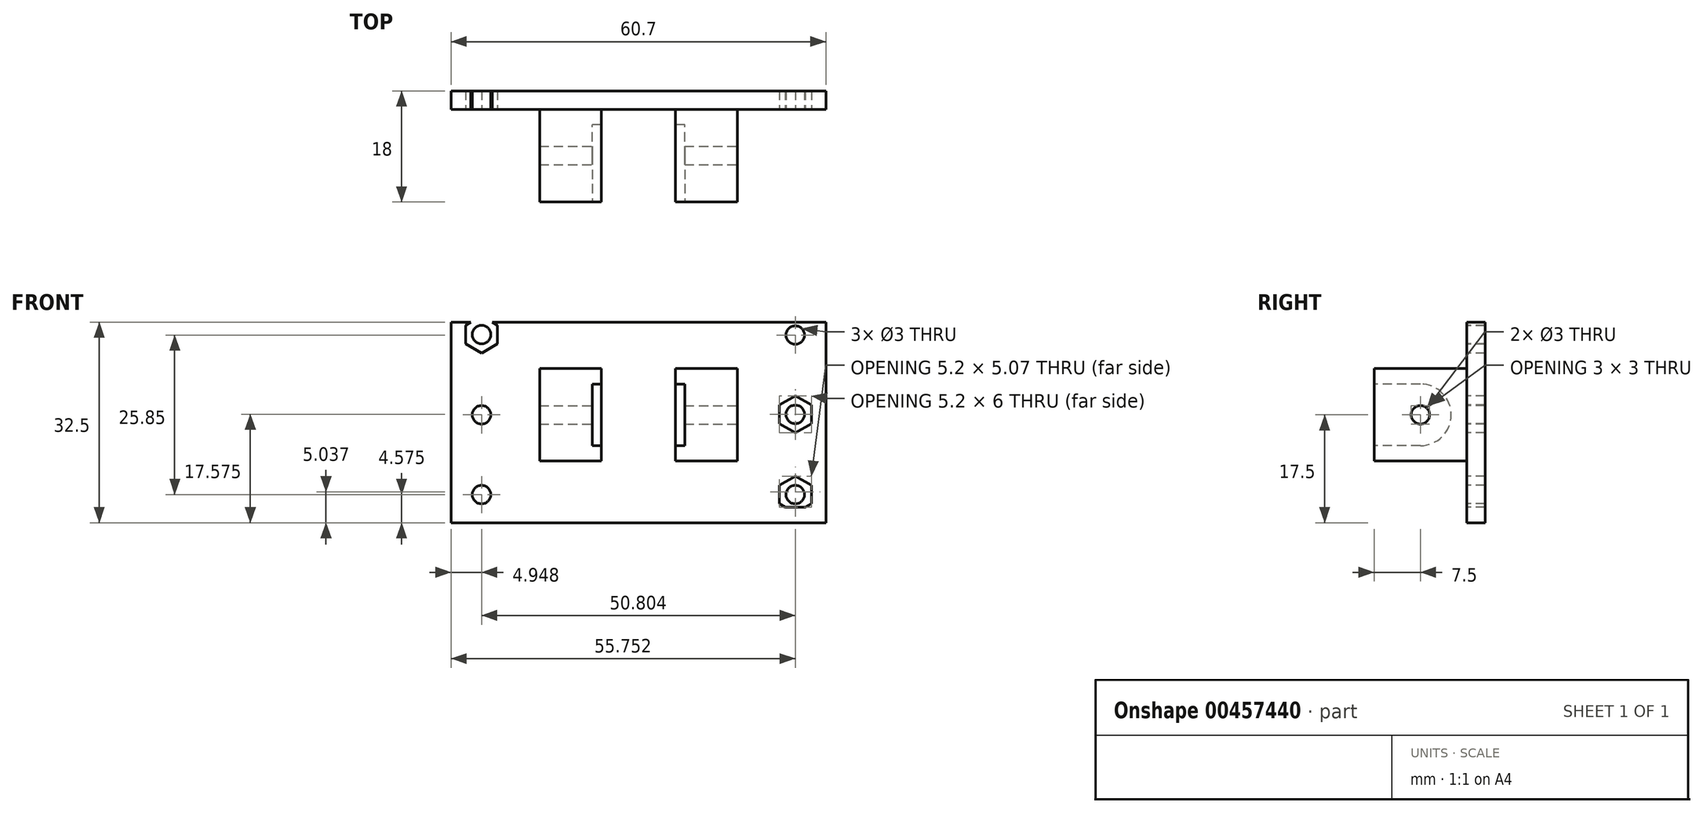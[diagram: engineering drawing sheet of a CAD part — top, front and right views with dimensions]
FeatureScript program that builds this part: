
annotation { "Feature Type Name" : "Feature", "Feature Type Description" : "" }
export const myFeature = defineFeature(function(context is Context, id is Id, definition is map)
    precondition{}
    {
        {
            var Q0;
            Q0=qCreatedBy(makeId("Front.planeOp"),FACE);
            var sketch = newSketch(context, id + "F0", { "sketchPlane" : qUnion([Q0])});
            skLineSegment(sketch, "E0.bottom", {"start": v(30, 15) * mm, "end": v(-30, 15) * mm});
            skLineSegment(sketch, "E0.top", {"start": v(30, -15) * mm, "end": v(-30, -15) * mm});
            skLineSegment(sketch, "E0.left", {"start": v(30, 15) * mm, "end": v(30, -15) * mm});
            skLineSegment(sketch, "E0.right", {"start": v(-30, 15) * mm, "end": v(-30, -15) * mm});
            skPoint(sketch, "E0.middle", {"position": v(0, 0) * mm});
            skSolve(sketch);
        }
        {
            var Q0;
            Q0=makeQuery(id+"F0.imprint","IMPRINT",FACE,{"disambiguationData":[TD([[makeQuery(id+"F0.imprint","IMPRINT",EDGE,{"derivedFrom":sQuery(id+"F0.wireOp",EDGE,"E0.bottom")}),1.0]])]});
            extrude(context, id + "F1", {"entities" : qUnion([Q0]), "endBound" : BoundingType.SYMMETRIC, "depth" : 3 * mm});
        }
        {
            var Q0;
            Q0=makeQuery(id+"F1.opExtrude","CAP_FACE",FACE,{"disambiguationData":[OSD([sQuery(id+"F0.wireOp",EDGE,"E0.bottom"),sQuery(id+"F0.wireOp",EDGE,"E0.top"),sQuery(id+"F0.wireOp",EDGE,"E0.left"),sQuery(id+"F0.wireOp",EDGE,"E0.right")])],"isStart":false});
            var sketch = newSketch(context, id + "F2", { "sketchPlane" : qUnion([Q0])});
            skCircle(sketch, "E1", {"center": v(-162.2, 7.5) * mm, "radius": 1.5 * mm});
            skCircle(sketch, "E2.MirrorC", {"center": v(-162.2, -7.5) * mm, "radius": 1.5 * mm});
            skLineSegment(sketch, "E3.0", {"start": v(-162.2, 10.5) * mm, "end": v(-159.6, 9) * mm});
            skLineSegment(sketch, "E3.1", {"start": v(-159.6, 9) * mm, "end": v(-159.6, 6) * mm});
            skLineSegment(sketch, "E3.2", {"start": v(-159.6, 6) * mm, "end": v(-162.2, 4.5) * mm});
            skLineSegment(sketch, "E3.3", {"start": v(-162.2, 4.5) * mm, "end": v(-164.8, 6) * mm});
            skLineSegment(sketch, "E3.4", {"start": v(-164.8, 6) * mm, "end": v(-164.8, 9) * mm});
            skLineSegment(sketch, "E3.5", {"start": v(-164.8, 9) * mm, "end": v(-162.2, 10.5) * mm});
            skLineSegment(sketch, "E4.MirrorCS", {"start": v(-162.2, -4.5) * mm, "end": v(-164.8, -6) * mm});
            skLineSegment(sketch, "E5.MirrorCS", {"start": v(-162.2, -10.5) * mm, "end": v(-159.6, -9) * mm});
            skLineSegment(sketch, "E6.MirrorCS", {"start": v(-164.8, -9) * mm, "end": v(-162.2, -10.5) * mm});
            skLineSegment(sketch, "E7.MirrorCS", {"start": v(-159.6, -9) * mm, "end": v(-159.6, -6) * mm});
            skLineSegment(sketch, "E8.MirrorCS", {"start": v(-164.8, -6) * mm, "end": v(-164.8, -9) * mm});
            skLineSegment(sketch, "E9.MirrorCS", {"start": v(-159.6, -6) * mm, "end": v(-162.2, -4.5) * mm});
            skLineSegment(sketch, "E10.MirrorCS", {"start": v(-162.2, 3) * mm, "end": v(-159.6, 1.5) * mm});
            skCircle(sketch, "E11.MirrorC", {"center": v(-162.2, 0) * mm, "radius": 1.5 * mm});
            skLineSegment(sketch, "E12.MirrorCS", {"start": v(-159.6, 1.5) * mm, "end": v(-159.6, -1.5) * mm});
            skLineSegment(sketch, "E13.MirrorCS", {"start": v(-162.2, -3) * mm, "end": v(-164.8, -1.5) * mm});
            skLineSegment(sketch, "E14.MirrorCS", {"start": v(-164.8, -1.5) * mm, "end": v(-164.8, 1.5) * mm});
            skLineSegment(sketch, "E15.MirrorCS", {"start": v(-159.6, -1.5) * mm, "end": v(-162.2, -3) * mm});
            skLineSegment(sketch, "E16.MirrorCS", {"start": v(-164.8, 1.5) * mm, "end": v(-162.2, 3) * mm});
            skLineSegment(sketch, "E17.MirrorCS", {"start": v(-22.8, 14.5) * mm, "end": v(-25.4, 16) * mm});
            skLineSegment(sketch, "E18.MirrorCS", {"start": v(-28, 11.5) * mm, "end": v(-25.4, 10) * mm});
            skLineSegment(sketch, "E19.MirrorCS", {"start": v(-25.4, -9.92) * mm, "end": v(-22.8, -11.42) * mm});
            skLineSegment(sketch, "E20.MirrorCS", {"start": v(-28, -11.42) * mm, "end": v(-25.4, -9.92) * mm});
            skLineSegment(sketch, "E21.MirrorCS", {"start": v(-25.4, -15.93) * mm, "end": v(-28, -14.43) * mm});
            skLineSegment(sketch, "E22.MirrorCS", {"start": v(-22.8, -14.43) * mm, "end": v(-25.4, -15.93) * mm});
            skLineSegment(sketch, "E23.MirrorCS", {"start": v(-25.4, 10) * mm, "end": v(-22.8, 11.5) * mm});
            skLineSegment(sketch, "E24.MirrorCS", {"start": v(-25.4, 16) * mm, "end": v(-28, 14.5) * mm});
            skLineSegment(sketch, "E25.MirrorCS", {"start": v(-22.8, 11.5) * mm, "end": v(-22.8, 14.5) * mm});
            skCircle(sketch, "E26.MirrorC", {"center": v(-25.4, 13) * mm, "radius": 1.5 * mm});
            skLineSegment(sketch, "E27.MirrorCS", {"start": v(-22.8, -11.42) * mm, "end": v(-22.8, -14.42) * mm});
            skLineSegment(sketch, "E28.MirrorCS", {"start": v(-28, 14.5) * mm, "end": v(-28, 11.5) * mm});
            skLineSegment(sketch, "E29.MirrorCS", {"start": v(-28, -14.42) * mm, "end": v(-28, -11.43) * mm});
            skCircle(sketch, "E30.MirrorC", {"center": v(-25.4, -12.92) * mm, "radius": 1.5 * mm});
            skPoint(sketch, "E31.endSnap0", {"position": v(-30, 0) * mm});
            skLineSegment(sketch, "E32.MirrorCS", {"start": v(25.4, 15.93) * mm, "end": v(28, 14.43) * mm});
            skLineSegment(sketch, "E33.MirrorCS", {"start": v(28, -11.42) * mm, "end": v(25.4, -9.92) * mm});
            skCircle(sketch, "E34.MirrorC", {"center": v(25.4, 12.93) * mm, "radius": 1.5 * mm});
            skLineSegment(sketch, "E35.MirrorCS", {"start": v(22.8, 14.43) * mm, "end": v(25.4, 15.93) * mm});
            skLineSegment(sketch, "E36.MirrorCS", {"start": v(25.4, 9.92) * mm, "end": v(22.8, 11.42) * mm});
            skLineSegment(sketch, "E37.MirrorCS", {"start": v(25.4, -9.92) * mm, "end": v(22.8, -11.42) * mm});
            skLineSegment(sketch, "E38.MirrorCS", {"start": v(28, -14.42) * mm, "end": v(28, -11.43) * mm});
            skLineSegment(sketch, "E39.MirrorCS", {"start": v(22.8, 11.42) * mm, "end": v(22.8, 14.42) * mm});
            skLineSegment(sketch, "E40.MirrorCS", {"start": v(25.4, -15.93) * mm, "end": v(28, -14.43) * mm});
            skLineSegment(sketch, "E41.MirrorCS", {"start": v(22.8, -11.42) * mm, "end": v(22.8, -14.42) * mm});
            skLineSegment(sketch, "E42.MirrorCS", {"start": v(28, 14.43) * mm, "end": v(28, 11.43) * mm});
            skLineSegment(sketch, "E43.MirrorCS", {"start": v(28, 11.42) * mm, "end": v(25.4, 9.92) * mm});
            skCircle(sketch, "E44.MirrorC", {"center": v(25.4, -12.92) * mm, "radius": 1.5 * mm});
            skLineSegment(sketch, "E45.MirrorCS", {"start": v(22.8, -14.43) * mm, "end": v(25.4, -15.93) * mm});
            skPoint(sketch, "E46.MirrorP", {"position": v(30, 0) * mm});
            skLineSegment(sketch, "E47.bottom", {"start": v(-6, 7.5) * mm, "end": v(6, 7.5) * mm});
            skLineSegment(sketch, "E47.top", {"start": v(-6, -7.5) * mm, "end": v(6, -7.5) * mm});
            skLineSegment(sketch, "E47.left", {"start": v(-6, 7.5) * mm, "end": v(-6, -7.5) * mm});
            skLineSegment(sketch, "E47.right", {"start": v(6, 7.5) * mm, "end": v(6, -7.5) * mm});
            skPoint(sketch, "E47.middle", {"position": v(0, 0) * mm});
            skLineSegment(sketch, "E48.bottom", {"start": v(6, -7.5) * mm, "end": v(16, -7.5) * mm});
            skLineSegment(sketch, "E48.top", {"start": v(6, 7.5) * mm, "end": v(16, 7.5) * mm});
            skLineSegment(sketch, "E48.left", {"start": v(6, -7.5) * mm, "end": v(6, 7.5) * mm});
            skLineSegment(sketch, "E48.right", {"start": v(16, -7.5) * mm, "end": v(16, 7.5) * mm});
            skLineSegment(sketch, "E49.MirrorCS", {"start": v(-6, -7.5) * mm, "end": v(-6, 7.5) * mm});
            skLineSegment(sketch, "E50.MirrorCS", {"start": v(-6, 7.5) * mm, "end": v(-16, 7.5) * mm});
            skLineSegment(sketch, "E51.MirrorCS", {"start": v(-16, -7.5) * mm, "end": v(-16, 7.5) * mm});
            skLineSegment(sketch, "E52.MirrorCS", {"start": v(-6, -7.5) * mm, "end": v(-16, -7.5) * mm});
            skLineSegment(sketch, "E53", {"start": v(-25.4, 17.5) * mm, "end": v(-25.4, 12.93) * mm});
            skLineSegment(sketch, "E54", {"start": v(-25.4, -17.5) * mm, "end": v(-25.4, -12.92) * mm});
            skLineSegment(sketch, "E55", {"start": v(-25.4, 0) * mm, "end": v(-25.4, 13) * mm});
            skLineSegment(sketch, "E56", {"start": v(-25.4, 6.5) * mm, "end": v(-21.98, 6.5) * mm});
            skLineSegment(sketch, "E57.MirrorCS", {"start": v(28, -1.42) * mm, "end": v(28, 1.58) * mm});
            skLineSegment(sketch, "E58.MirrorCS", {"start": v(22.8, 1.58) * mm, "end": v(22.8, -1.42) * mm});
            skLineSegment(sketch, "E59.MirrorCS", {"start": v(28, 1.58) * mm, "end": v(25.4, 3.08) * mm});
            skLineSegment(sketch, "E60.MirrorCS", {"start": v(25.4, -2.92) * mm, "end": v(28, -1.42) * mm});
            skLineSegment(sketch, "E61.MirrorCS", {"start": v(25.4, 3.08) * mm, "end": v(22.8, 1.58) * mm});
            skLineSegment(sketch, "E62.MirrorCS", {"start": v(22.8, -1.42) * mm, "end": v(25.4, -2.93) * mm});
            skCircle(sketch, "E63.MirrorC", {"center": v(25.4, 0.08) * mm, "radius": 1.5 * mm});
            skLineSegment(sketch, "E64.MirrorCS", {"start": v(-22.8, -1.5) * mm, "end": v(-25.4, -3) * mm});
            skLineSegment(sketch, "E65.MirrorCS", {"start": v(-25.4, -3) * mm, "end": v(-28, -1.5) * mm});
            skCircle(sketch, "E66.MirrorC", {"center": v(-25.4, 0) * mm, "radius": 1.5 * mm});
            skLineSegment(sketch, "E67.MirrorCS", {"start": v(-28, -1.5) * mm, "end": v(-28, 1.5) * mm});
            skLineSegment(sketch, "E68.MirrorCS", {"start": v(-25.4, 3) * mm, "end": v(-22.8, 1.5) * mm});
            skLineSegment(sketch, "E69.MirrorCS", {"start": v(-22.8, 1.5) * mm, "end": v(-22.8, -1.5) * mm});
            skLineSegment(sketch, "E70.MirrorCS", {"start": v(-28, 1.5) * mm, "end": v(-25.4, 3) * mm});
            skSolve(sketch);
        }
        {
            var Q0;
            Q0=makeQuery(id+"F2.imprint","IMPRINT",FACE,{"disambiguationData":[TD([[makeQuery(id+"F2.imprint","IMPRINT",EDGE,{"derivedFrom":sQuery(id+"F2.wireOp",EDGE,"E50.MirrorCS")}),1.0]])]});
            var Q1;
            Q1=makeQuery(id+"F2.imprint","IMPRINT",FACE,{"disambiguationData":[TD([[makeQuery(id+"F2.imprint","IMPRINT",EDGE,{"derivedFrom":sQuery(id+"F2.wireOp",EDGE,"E48.bottom")}),1.0]])]});
            extrude(context, id + "F3", {"entities" : qUnion([Q0, Q1]), "operationType" : NewBodyOperationType.ADD, "depth" : 15 * mm});
        }
        {
            var Q0;
            Q0=makeQuery(id+"F2.imprint","IMPRINT",FACE,{"disambiguationData":[TD([[makeQuery(id+"F2.imprint","IMPRINT",EDGE,{"derivedFrom":sQuery(id+"F2.wireOp",EDGE,"E26.MirrorC")}),-1.0]])]});
            var Q1;
            Q1=makeQuery(id+"F2.imprint","IMPRINT",FACE,{"disambiguationData":[TD([[makeQuery(id+"F2.imprint","IMPRINT",EDGE,{"derivedFrom":sQuery(id+"F2.wireOp",EDGE,"E30.MirrorC")}),1.0]])]});
            var Q2;
            Q2=makeQuery(id+"F2.imprint","IMPRINT",FACE,{"disambiguationData":[TD([[makeQuery(id+"F2.imprint","IMPRINT",EDGE,{"derivedFrom":sQuery(id+"F2.wireOp",EDGE,"E34.MirrorC")}),1.0]])]});
            var Q3;
            Q3=makeQuery(id+"F2.imprint","IMPRINT",FACE,{"disambiguationData":[TD([[makeQuery(id+"F2.imprint","IMPRINT",EDGE,{"derivedFrom":sQuery(id+"F2.wireOp",EDGE,"E44.MirrorC")}),-1.0]])]});
            var Q4;
            Q4=makeQuery(id+"F2.imprint","IMPRINT",FACE,{"disambiguationData":[TD([[makeQuery(id+"F2.imprint","IMPRINT",EDGE,{"derivedFrom":sQuery(id+"F2.wireOp",EDGE,"E66.MirrorC")}),1.0]])]});
            var Q5;
            Q5=makeQuery(id+"F2.imprint","IMPRINT",FACE,{"disambiguationData":[TD([[makeQuery(id+"F2.imprint","IMPRINT",EDGE,{"derivedFrom":sQuery(id+"F2.wireOp",EDGE,"E63.MirrorC")}),-1.0]])]});
            extrude(context, id + "F4", {"entities" : qUnion([Q0, Q1, Q2, Q3, Q4, Q5]), "operationType" : NewBodyOperationType.REMOVE, "oppositeDirection" : true, "depth" : 3 * mm});
        }
        {
            var Q0;
            Q0=qCreatedBy(makeId("Right.planeOp"),FACE);
            var sketch = newSketch(context, id + "F5", { "sketchPlane" : qUnion([Q0])});
            skPoint(sketch, "E71.0", {"position": v(-16.5, 0) * mm});
            skPoint(sketch, "E72.0", {"position": v(-9, 7.5) * mm});
            skCircle(sketch, "E73", {"center": v(-9, 0) * mm, "radius": 1.5 * mm});
            skCircle(sketch, "E74", {"center": v(-9, 0) * mm, "radius": 5 * mm});
            skSolve(sketch);
        }
        {
            var Q0;
            Q0=makeQuery(id+"F5.imprint","IMPRINT",FACE,{"disambiguationData":[TD([[makeQuery(id+"F5.imprint","IMPRINT",EDGE,{"derivedFrom":sQuery(id+"F5.wireOp",EDGE,"E73")}),-1.0]])]});
            extrude(context, id + "F6", {"entities" : qUnion([Q0]), "operationType" : NewBodyOperationType.REMOVE, "endBound" : BoundingType.SYMMETRIC, "depth" : 15 * mm});
        }
        {
            var Q0;
            Q0=makeQuery(id+"F6.boolean.opBoolean","SPLIT",FACE,{"disambiguationData":[TD([makeQuery(id+"F6.opExtrude","SWEPT_FACE",FACE,{"disambiguationData":[OSD([sQuery(id+"F5.wireOp",EDGE,"E73")])]})])],"derivedFrom":makeQuery(id+"F3.opExtrude","SWEPT_FACE",FACE,{"disambiguationData":[OSD([sQuery(id+"F2.wireOp",EDGE,"E47.left")])]})});
            extrude(context, id + "F7", {"entities" : qUnion([Q0]), "operationType" : NewBodyOperationType.REMOVE, "endBound" : BoundingType.SYMMETRIC, "oppositeDirection" : true, "depth" : 60 * mm});
        }
        {
            var Q0;
            Q0=qCreatedBy(makeId("Right.planeOp"),FACE);
            var sketch = newSketch(context, id + "F8", { "sketchPlane" : qUnion([Q0])});
            skLineSegment(sketch, "E75.0", {"start": v(-16.5, 5) * mm, "end": v(-16.5, -5) * mm});
            skLineSegment(sketch, "E76", {"start": v(-9, 0) * mm, "end": v(-9, 5) * mm});
            skLineSegment(sketch, "E77", {"start": v(-9, 5) * mm, "end": v(-16.5, 5) * mm});
            skLineSegment(sketch, "E78", {"start": v(-9, 0) * mm, "end": v(-9, -5) * mm});
            skLineSegment(sketch, "E79", {"start": v(-9, -5) * mm, "end": v(-16.5, -5) * mm});
            skSolve(sketch);
        }
        {
            var Q0;
            Q0=makeQuery(id+"F8.imprint","IMPRINT",FACE,{"disambiguationData":[TD([[makeQuery(id+"F8.imprint","IMPRINT",EDGE,{"derivedFrom":sQuery(id+"F8.wireOp",EDGE,"E75.0")}),1.0]])]});
            extrude(context, id + "F9", {"entities" : qUnion([Q0]), "operationType" : NewBodyOperationType.REMOVE, "endBound" : BoundingType.SYMMETRIC, "oppositeDirection" : true, "depth" : 15 * mm});
        }
        {
            var Q0;
            Q0=makeQuery(id+"F1.opExtrude","CAP_FACE",FACE,{"disambiguationData":[OSD([sQuery(id+"F0.wireOp",EDGE,"E0.bottom"),sQuery(id+"F0.wireOp",EDGE,"E0.top"),sQuery(id+"F0.wireOp",EDGE,"E0.left"),sQuery(id+"F0.wireOp",EDGE,"E0.right")])],"isStart":true});
            var sketch = newSketch(context, id + "F10", { "sketchPlane" : qUnion([Q0])});
            skCircle(sketch, "E80.0", {"center": v(-25.4, -12.92) * mm, "radius": 1.5 * mm});
            skLineSegment(sketch, "E81.0", {"start": v(-30, 15) * mm, "end": v(-30, -15) * mm});
            skLineSegment(sketch, "E82", {"start": v(-25.4, -12.92) * mm, "end": v(-30.35, -12.92) * mm});
            skLineSegment(sketch, "E83.bottom", {"start": v(-30.35, -15) * mm, "end": v(-30, -15) * mm});
            skLineSegment(sketch, "E83.top", {"start": v(-30.35, 15) * mm, "end": v(-30, 15) * mm});
            skLineSegment(sketch, "E83.left", {"start": v(-30.35, -15) * mm, "end": v(-30.35, 15) * mm});
            skLineSegment(sketch, "E83.right", {"start": v(-30, -15) * mm, "end": v(-30, 15) * mm});
            skLineSegment(sketch, "E84", {"start": v(0, -15) * mm, "end": v(0, 0) * mm});
            skLineSegment(sketch, "E85.MirrorCS", {"start": v(30.35, -15) * mm, "end": v(30, -15) * mm});
            skLineSegment(sketch, "E86.MirrorCS", {"start": v(30.35, 15) * mm, "end": v(30, 15) * mm});
            skLineSegment(sketch, "E87.MirrorCS", {"start": v(30, 15) * mm, "end": v(30, -15) * mm});
            skLineSegment(sketch, "E88.MirrorCS", {"start": v(30, -15) * mm, "end": v(30, 15) * mm});
            skLineSegment(sketch, "E89.MirrorCS", {"start": v(30.35, -15) * mm, "end": v(30.35, 15) * mm});
            skLineSegment(sketch, "E90.0", {"start": v(-30, -15) * mm, "end": v(30, -15) * mm});
            skLineSegment(sketch, "E91.0", {"start": v(-30, 15) * mm, "end": v(30, 15) * mm});
            skLineSegment(sketch, "E92", {"start": v(-25.4, -15) * mm, "end": v(-25.4, -10.43) * mm});
            skSolve(sketch);
        }
        {
            var Q0;
            Q0=makeQuery(id+"F10.imprint","IMPRINT",FACE,{"disambiguationData":[TD([[makeQuery(id+"F10.imprint","IMPRINT",EDGE,{"derivedFrom":sQuery(id+"F10.wireOp",EDGE,"E85.MirrorCS")}),-1.0]])]});
            var Q1;
            {var subQ5=sQuery(id+"F10.wireOp",EDGE,"E83.bottom");Q1=makeQuery(id+"F10.imprint","IMPRINT",FACE,{"disambiguationData":[TD([[makeQuery(id+"F10.imprint","IMPRINT",EDGE,{"derivedFrom":subQ5}),1.0]])]});}
            var Q2;
            {var subQ5=sQuery(id+"F10.wireOp",EDGE,"E83.top");Q2=makeQuery(id+"F10.imprint","IMPRINT",FACE,{"disambiguationData":[TD([[makeQuery(id+"F10.imprint","IMPRINT",EDGE,{"derivedFrom":subQ5}),-1.0]])]});}
            extrude(context, id + "F11", {"entities" : qUnion([Q0, Q1, Q2]), "operationType" : NewBodyOperationType.ADD, "depth" : -3 * mm});
        }
        {
            var Q0;
            Q0=makeQuery(id+"F11.boolean.opBoolean","MERGE",FACE,{"derivedFrom":[makeQuery(id+"F1.opExtrude","CAP_FACE",FACE,{"disambiguationData":[OSD([sQuery(id+"F0.wireOp",EDGE,"E0.bottom"),sQuery(id+"F0.wireOp",EDGE,"E0.top"),sQuery(id+"F0.wireOp",EDGE,"E0.left"),sQuery(id+"F0.wireOp",EDGE,"E0.right")])],"isStart":true}),makeQuery(id+"F11.opExtrude","CAP_FACE",FACE,{"disambiguationData":[OSD([sQuery(id+"F10.wireOp",EDGE,"E83.bottom"),sQuery(id+"F10.wireOp",EDGE,"E83.top"),sQuery(id+"F10.wireOp",EDGE,"E83.left"),sQuery(id+"F10.wireOp",EDGE,"E83.right")])],"isStart":true}),makeQuery(id+"F11.opExtrude","CAP_FACE",FACE,{"disambiguationData":[OSD([sQuery(id+"F10.wireOp",EDGE,"E85.MirrorCS"),sQuery(id+"F10.wireOp",EDGE,"E86.MirrorCS"),sQuery(id+"F10.wireOp",EDGE,"E88.MirrorCS"),sQuery(id+"F10.wireOp",EDGE,"E89.MirrorCS")])],"isStart":true})]});
            var sketch = newSketch(context, id + "F12", { "sketchPlane" : qUnion([Q0])});
            skPoint(sketch, "E93.0", {"position": v(-30.35, 15) * mm});
            skLineSegment(sketch, "E94.0", {"start": v(-30.35, 15) * mm, "end": v(30.35, 15) * mm});
            skLineSegment(sketch, "E95.0", {"start": v(-30.35, -15) * mm, "end": v(30.35, -15) * mm});
            skCircle(sketch, "E96.0.0", {"center": v(-25.4, -12.92) * mm, "radius": 1.5 * mm});
            skLineSegment(sketch, "E97.top", {"start": v(-30.35, 17.5) * mm, "end": v(30.35, 17.5) * mm});
            skLineSegment(sketch, "E97.left", {"start": v(-30.35, 15) * mm, "end": v(-30.35, 17.5) * mm});
            skLineSegment(sketch, "E97.right", {"start": v(30.35, 15) * mm, "end": v(30.35, 17.5) * mm});
            skLineSegment(sketch, "E98.MirrorCS", {"start": v(30.35, -15) * mm, "end": v(30.35, -17.5) * mm});
            skPoint(sketch, "E99.MirrorP", {"position": v(-30.35, -15) * mm});
            skLineSegment(sketch, "E100.MirrorCS", {"start": v(-30.35, -15) * mm, "end": v(-30.35, -17.5) * mm});
            skLineSegment(sketch, "E101.MirrorCS", {"start": v(-30.35, -17.5) * mm, "end": v(30.35, -17.5) * mm});
            skSolve(sketch);
        }
        {
            var Q0;
            Q0=makeQuery(id+"F12.imprint","IMPRINT",FACE,{"disambiguationData":[TD([[makeQuery(id+"F12.imprint","IMPRINT",EDGE,{"derivedFrom":sQuery(id+"F12.wireOp",EDGE,"E94.0")}),1.0]])]});
            var Q1;
            Q1=makeQuery(id+"F12.imprint","IMPRINT",FACE,{"disambiguationData":[TD([[makeQuery(id+"F12.imprint","IMPRINT",EDGE,{"derivedFrom":sQuery(id+"F12.wireOp",EDGE,"E98.MirrorCS")}),-1.0]])]});
            extrude(context, id + "F13", {"entities" : qUnion([Q0, Q1]), "operationType" : NewBodyOperationType.ADD, "depth" : -3 * mm});
        }
    });
